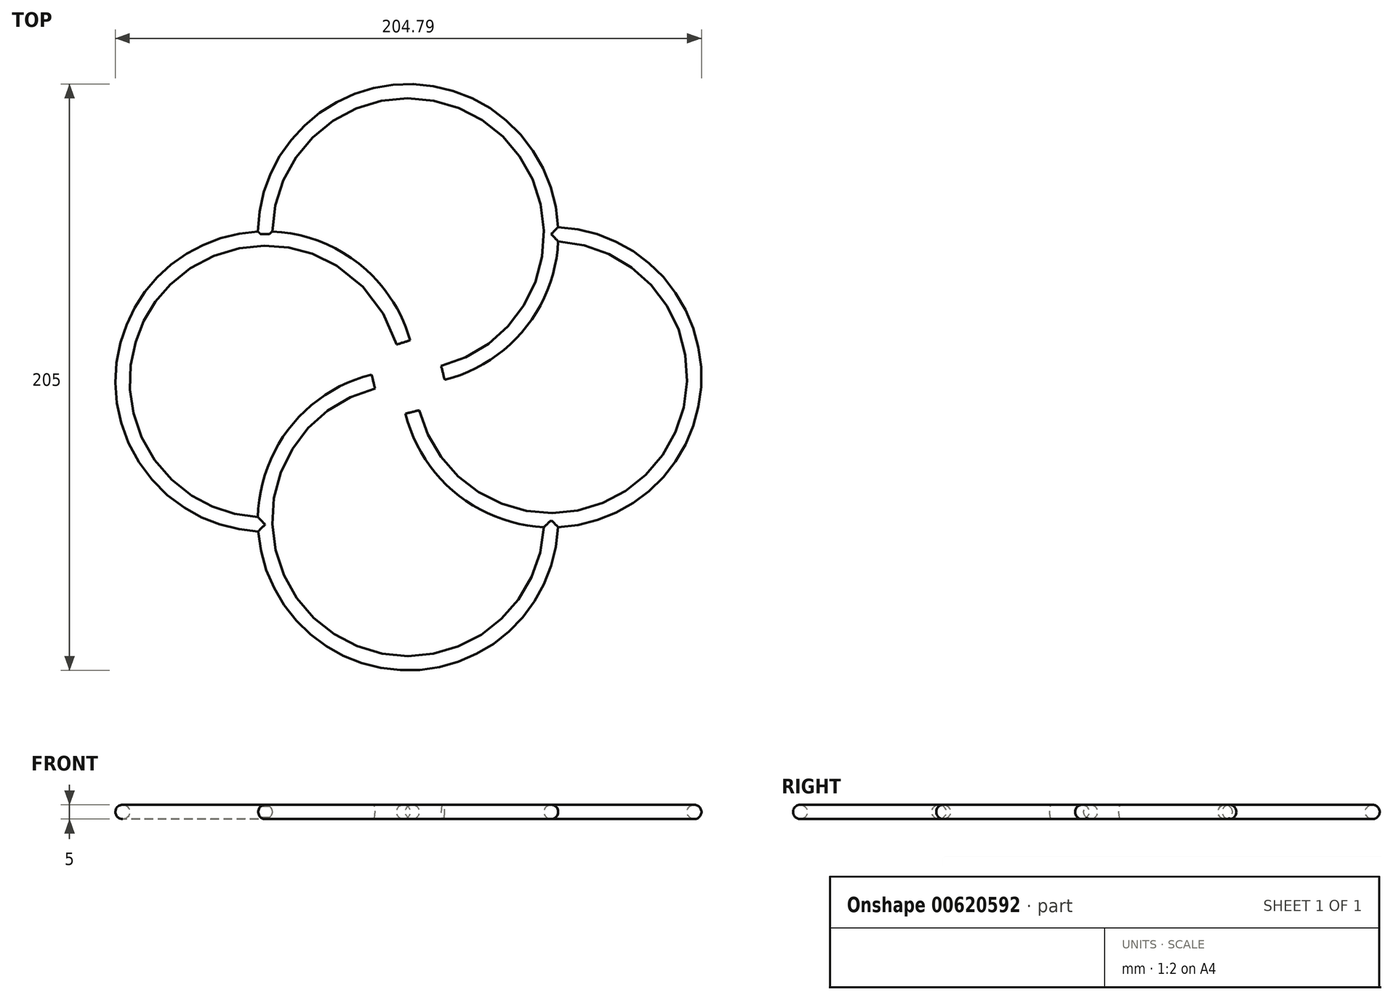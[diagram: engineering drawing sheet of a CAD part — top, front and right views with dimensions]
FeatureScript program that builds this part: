
annotation { "Feature Type Name" : "Feature", "Feature Type Description" : "" }
export const myFeature = defineFeature(function(context is Context, id is Id, definition is map)
    precondition{}
    {
        {
            var Q0;
            Q0=qCreatedBy(makeId("Top.planeOp"),FACE);
            var sketch = newSketch(context, id + "F0", { "sketchPlane" : qUnion([Q0])});
            skCircle(sketch, "E0", {"center": v(0, 0) * mm, "radius": 12.25 * mm});
            skPoint(sketch, "E1.second.point", {"position": v(-73.8, -33.5) * mm});
            skPoint(sketch, "E1.third.point", {"position": v(-34.8, -43.43) * mm});
            skArc(sketch, "E2", {"start": v(-12.16, -1.5) * mm, "mid": v(-30.76, -89.42) * mm, "end": v(50, -50) * mm});
            skPoint(sketch, "E2.second.point", {"position": v(0, -100) * mm});
            skPoint(sketch, "E2.third.point", {"position": v(44.5, -72.8) * mm});
            skArc(sketch, "E3", {"start": v(1.5, -12.16) * mm, "mid": v(89.42, -30.76) * mm, "end": v(50, 50) * mm});
            skPoint(sketch, "E3.second.point", {"position": v(100, 0) * mm});
            skPoint(sketch, "E3.third.point", {"position": v(72.81, -44.5) * mm});
            skArc(sketch, "E4", {"start": v(12.16, 1.5) * mm, "mid": v(30.76, 89.42) * mm, "end": v(-50, 50) * mm});
            skPoint(sketch, "E4.second.point", {"position": v(0, 100) * mm});
            skPoint(sketch, "E4.third.point", {"position": v(-37.22, 83.38) * mm});
            skArc(sketch, "E5.trimOffspring", {"start": v(-1.69, 12.13) * mm, "mid": v(-89.62, 28.73) * mm, "end": v(-49.98, -51.5) * mm});
            skPoint(sketch, "E1.center.orphan", {"position": v(-44.5, 0) * mm});
            skCircle(sketch, "E6", {"center": v(0, 0) * mm, "radius": 12.94 * mm});
            skSolve(sketch);
        }
        {
            var Q0;
            Q0=qCreatedBy(makeId("Front.planeOp"),FACE);
            var sketch = newSketch(context, id + "F1", { "sketchPlane" : qUnion([Q0])});
            skCircle(sketch, "E7", {"center": v(100, 0) * mm, "radius": 2.5 * mm});
            skCircle(sketch, "E8", {"center": v(-99.78, 0) * mm, "radius": 2.5 * mm});
            skSolve(sketch);
        }
        {
            var Q0;
            Q0=qCreatedBy(makeId("Right.planeOp"),FACE);
            var sketch = newSketch(context, id + "F2", { "sketchPlane" : qUnion([Q0])});
            skCircle(sketch, "E9", {"center": v(100, 0) * mm, "radius": 2.5 * mm});
            skCircle(sketch, "E10", {"center": v(-100, 0) * mm, "radius": 2.5 * mm});
            skSolve(sketch);
        }
        {
            var Q0;
            Q0=makeQuery(id+"F2.imprint","IMPRINT",FACE,{"disambiguationData":[TD([[makeQuery(id+"F2.imprint","IMPRINT",EDGE,{"derivedFrom":sQuery(id+"F2.wireOp",EDGE,"E9")}),1.0]])]});
            var Q1;
            Q1=sQuery(id+"F0.wireOp",EDGE,"E4");
            sweep(context, id + "F3", {"profiles" : qUnion([Q0]), "path" : qUnion([Q1])});
        }
        {
            var Q0;
            Q0=makeQuery(id+"F1.imprint","IMPRINT",FACE,{"disambiguationData":[TD([[makeQuery(id+"F1.imprint","IMPRINT",EDGE,{"derivedFrom":sQuery(id+"F1.wireOp",EDGE,"E7")}),1.0]])]});
            var Q1;
            Q1=sQuery(id+"F0.wireOp",EDGE,"E3");
            sweep(context, id + "F4", {"operationType" : NewBodyOperationType.ADD, "profiles" : qUnion([Q0]), "path" : qUnion([Q1])});
        }
        {
            var Q0;
            Q0=makeQuery(id+"F2.imprint","IMPRINT",FACE,{"disambiguationData":[TD([[makeQuery(id+"F2.imprint","IMPRINT",EDGE,{"derivedFrom":sQuery(id+"F2.wireOp",EDGE,"E10")}),1.0]])]});
            var Q1;
            Q1=sQuery(id+"F0.wireOp",EDGE,"E2");
            sweep(context, id + "F5", {"operationType" : NewBodyOperationType.ADD, "profiles" : qUnion([Q0]), "path" : qUnion([Q1])});
        }
        {
            var Q0;
            Q0=makeQuery(id+"F1.imprint","IMPRINT",FACE,{"disambiguationData":[TD([[makeQuery(id+"F1.imprint","IMPRINT",EDGE,{"derivedFrom":sQuery(id+"F1.wireOp",EDGE,"E8")}),1.0]])]});
            var Q1;
            Q1=sQuery(id+"F0.wireOp",EDGE,"E5.trimOffspring");
            sweep(context, id + "F6", {"operationType" : NewBodyOperationType.ADD, "profiles" : qUnion([Q0]), "path" : qUnion([Q1])});
        }
    });
